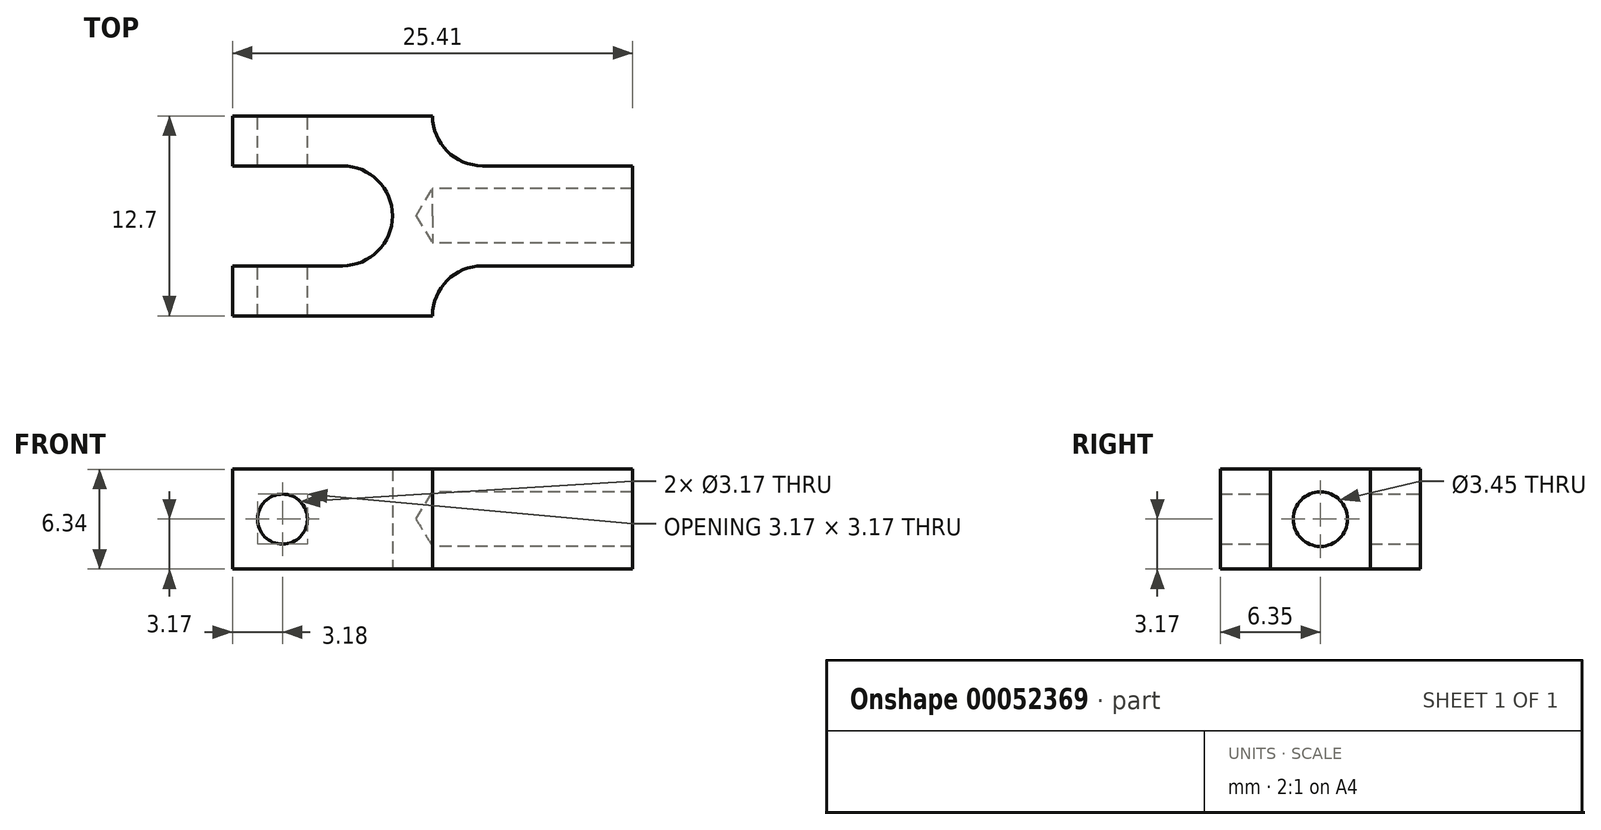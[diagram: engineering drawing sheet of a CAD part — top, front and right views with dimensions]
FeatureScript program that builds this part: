
annotation { "Feature Type Name" : "Feature", "Feature Type Description" : "" }
export const myFeature = defineFeature(function(context is Context, id is Id, definition is map)
    precondition{}
    {
        {
            var Q0;
            Q0=qCreatedBy(makeId("Top.planeOp"),FACE);
            var sketch = newSketch(context, id + "F0", { "sketchPlane" : qUnion([Q0])});
            skLineSegment(sketch, "E0", {"start": v(-6.98, -3.18) * mm, "end": v(-6.98, -6.35) * mm});
            skLineSegment(sketch, "E1", {"start": v(-6.99, -6.35) * mm, "end": v(5.72, -6.35) * mm});
            skArc(sketch, "E2", {"start": v(0, 3.18) * mm, "mid": v(3.18, 0) * mm, "end": v(0, -3.18) * mm});
            skLineSegment(sketch, "E3", {"start": v(0, -3.18) * mm, "end": v(-6.98, -3.18) * mm});
            skLineSegment(sketch, "E4", {"start": v(0, 3.18) * mm, "end": v(-6.98, 3.18) * mm});
            skLineSegment(sketch, "E5", {"start": v(-6.99, 3.18) * mm, "end": v(-6.99, 6.35) * mm});
            skLineSegment(sketch, "E6", {"start": v(-6.98, 6.35) * mm, "end": v(5.72, 6.35) * mm});
            skLineSegment(sketch, "E7", {"start": v(8.9, -3.18) * mm, "end": v(18.41, -3.18) * mm});
            skLineSegment(sketch, "E8", {"start": v(18.41, -3.18) * mm, "end": v(18.41, 3.18) * mm});
            skLineSegment(sketch, "E9", {"start": v(18.41, 3.18) * mm, "end": v(8.9, 3.18) * mm});
            skPoint(sketch, "E10", {"position": v(18.41, 0) * mm});
            skArc(sketch, "E11", {"start": v(8.9, 3.17) * mm, "mid": v(6.64, 4.1) * mm, "end": v(5.72, 6.35) * mm});
            skArc(sketch, "E12", {"start": v(8.9, -3.18) * mm, "mid": v(6.64, -4.1) * mm, "end": v(5.72, -6.35) * mm});
            skSolve(sketch);
        }
        {
            var Q0;
            Q0 = qSketchRegion(id + "F0", true);
            extrude(context, id + "F1", {"entities" : qUnion([Q0]), "depth" : 6.35 * mm, "symmetric" : true});
        }
        {
            var Q0;
            Q0=makeQuery(id+"F1.opExtrude","SWEPT_FACE",FACE,{"disambiguationData":[OSD([sQuery(id+"F0.wireOp",EDGE,"E8")])]});
            var sketch = newSketch(context, id + "F2", { "sketchPlane" : qUnion([Q0])});
            skPoint(sketch, "E13", {"position": v(0, 0) * mm});
            skSolve(sketch);
        }
        {
            var Q0;
            Q0=sQuery(id+"F2.wireOp",VERTEX,"E13");
            var Q1;
            Q1=makeQuery(id+"F1.opExtrude","SWEPT_BODY",BODY,{"disambiguationData":[OSD([sQuery(id+"F0.wireOp",EDGE,"E0"),sQuery(id+"F0.wireOp",EDGE,"E1"),sQuery(id+"F0.wireOp",EDGE,"E2"),sQuery(id+"F0.wireOp",EDGE,"E3"),sQuery(id+"F0.wireOp",EDGE,"E4"),sQuery(id+"F0.wireOp",EDGE,"E5"),sQuery(id+"F0.wireOp",EDGE,"E6"),sQuery(id+"F0.wireOp",EDGE,"E7"),sQuery(id+"F0.wireOp",EDGE,"E8"),sQuery(id+"F0.wireOp",EDGE,"E9"),sQuery(id+"F0.wireOp",EDGE,"E11"),sQuery(id+"F0.wireOp",EDGE,"E12")])]});
            hole(context, id + "F3", {"style" : HoleStyle.SIMPLE, "holeDiameter" : 3.45 * mm, "endStyle" : HoleEndStyle.BLIND, "holeDepth" : 12.7 * mm, "locations" : qUnion([Q0]), "scope" : qUnion([Q1])});
        }
        {
            var Q0;
            Q0=makeQuery(id+"F1.opExtrude","SWEPT_FACE",FACE,{"disambiguationData":[OSD([sQuery(id+"F0.wireOp",EDGE,"E1")])]});
            var sketch = newSketch(context, id + "F4", { "sketchPlane" : qUnion([Q0])});
            skPoint(sketch, "E14", {"position": v(-3.81, 0) * mm});
            skSolve(sketch);
        }
        {
            var Q0;
            Q0=sQuery(id+"F4.wireOp",VERTEX,"E14");
            var Q1;
            Q1=makeQuery(id+"F1.opExtrude","SWEPT_BODY",BODY,{"disambiguationData":[OSD([sQuery(id+"F0.wireOp",EDGE,"E0"),sQuery(id+"F0.wireOp",EDGE,"E1"),sQuery(id+"F0.wireOp",EDGE,"E2"),sQuery(id+"F0.wireOp",EDGE,"E3"),sQuery(id+"F0.wireOp",EDGE,"E4"),sQuery(id+"F0.wireOp",EDGE,"E5"),sQuery(id+"F0.wireOp",EDGE,"E6"),sQuery(id+"F0.wireOp",EDGE,"E7"),sQuery(id+"F0.wireOp",EDGE,"E8"),sQuery(id+"F0.wireOp",EDGE,"E9"),sQuery(id+"F0.wireOp",EDGE,"E11"),sQuery(id+"F0.wireOp",EDGE,"E12")])]});
            hole(context, id + "F5", {"style" : HoleStyle.SIMPLE, "holeDiameter" : 3.17 * mm, "endStyle" : HoleEndStyle.THROUGH, "locations" : qUnion([Q0]), "scope" : qUnion([Q1])});
        }
    });
